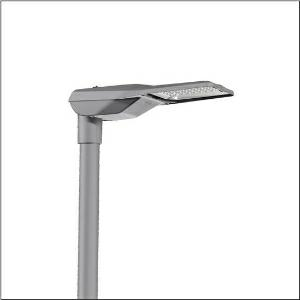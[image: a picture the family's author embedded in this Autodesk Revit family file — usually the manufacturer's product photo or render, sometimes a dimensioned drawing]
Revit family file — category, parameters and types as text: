
# Revit family: streetlight_sl_21_mini___stw1_0a_5xe2e33s08gb_da95
name_source: partatom
category: Lighting Fixtures
units: mm (PartAtom-declared; Revit-internal decimal feet)

## family parameters
Cut with Voids When Loaded = No
Host = Face
Light Source = No
Part Type = Normal
Room Calculation Point = No
Round Connector Dimension = Use Diameter
Shared = No

## types (1)
- --- (1 x LED, 5940 lm, 40.4 W, 3000K)
    Apparent Load = 40 VA
    CIE Flux Codes = 38 75 98 100 100
    Color Rendering = 70
    Color Temperature = 3000K
    Default Elevation = 1800 mm
    Description = Streetlight SL 21 mini, mast luminaire, primary light control with lens, of PMMA, primary optical cover: cover, of toughened safety glass, transparent, light distribution: STW1.0a, light emission: direct distribution, primary light characteristic: asymmetric, installation type: side-entry, post-top, LED, High Power LED, rated luminous flux: 5.940lm, luminous efficacy: 147lm/W, light colour: 730, colour temperature: 3000K, control gear: D4i, control: overheat protection, constant luminous flux control, time-dependent luminous flux control, flexible luminous flux parameterisation, pre-setting: logarithmic dimming characteristic, mains connection: 220..240V, AC, 50/60Hz, start of lifetime: 40W, end of service life: 41W, reduction: 19W, luminaire housing, of diecast aluminium, powder-coated, SITECO metallic grey (DB 702S), corrosivity category C5 high according to DIN EN ISO 12944, please order mast flange separately, inclination adjustable: 0°, 5°, 10°, 15°, sealing non-destructively replaceable, multi-level sealing system, length: 628mm, width: 235mm, height: 110mm, mast flange for spigot size: 42mm (side-entry): 5XC10008XM4, 60/48mm (side-entry/post-top): 5XC10108XM2, 76/60mm (side-entry/post-top): 5XC10108XM1, mounting height: 4..8m, Smart Interface above, protection rating (complete): IP66, insulation class (complete): insulation class II (safety insulation), certification: CE, ENEC, ENEC+, VDE, impact resistance: IK10, permissible operating ambient temperature for outdoor applications: -40..+50°C, standard-compliant lighting for roads and squares, packaging unit: 1 piece

Light Distribution: STW1.0a
    Height = 110 mm
    Lamp = 1 x LED
    Lamp Light Flux = 5940 lm
    Lamp Power = 40.4 W
    Lamp count = 1
    Length = 625 mm
    Luminous efficacy = 147 lm/W
    Manufacturer = Siteco
    ModVariant = No
    Model = 5XE2E33S08GB
    Number of Poles = 1
    OnlyDefault = Yes
    Power Factor = 1
    Product Name = Streetlight SL 21 mini | STW1.0a
    Product group = mast luminaire | pylon top
    ProductGroupID = 6100
    Protection Class = Protection class II
    Protection Degree = IP 66
    RLX_Detail_Level = 1
    RLX_Emergency_Light_Flux = 0 lm
    RLX_Emergency_Type = 0
    RLX_Emergency_Type_DB = No
    RlxData = <blob elided: 26221 chars, md5=4cc6e237>
    Socket = socket
    Standby Power = 0 W
    System Light Flux = 5940 lm
    System Power = 40 W
    Type Comments = factory setting: luminous flux: 100 % | dim-lin: 254 | 812 mA
    Type Image = l_1003515.jpg
    URL = http://relux.com
    VarID = @adj_184909
    Voltage = 0 V
    Weight = 0.00 kg
    Width = 234 mm

## geometry (parser evidence)
native form markers: Blend x4, Sweep x12
no freeform markers — native parametric forms only
